# Revit family: HFS
name_source: partatom
category: Duct Accessories
revit_build: Autodesk Revit 2014 (Build: 20130308_1515(x64)
units: mm (PartAtom-declared; Revit-internal decimal feet)

## types (1)
- HFS
    A = 132 mm
    A Min = 115 mm
    Actuator Material = Aluminium
    Actuator Width = 523 mm
    Array = 5
    B = 50 mm
    B Min = 33 mm
    Blade Spacing = 146 mm  [stored 0.479003 ft]
    Blade W = 466 mm  [stored 1.52887 ft]
    Blades = 5
    C = 747 mm
    C Min = 613 mm
    Frame Allowance = 23 mm  [stored 0.0754593 ft]
    Frame Edge = 6 mm  [stored 0.019685 ft]
    Frame Material = Aluminium
    H Min = 814 mm  [stored 2.6706 ft]
    Internal Duct H = 894 mm
    Internal Duct W = 494 mm
    Manufacturer = Holyoake Industries
    Model = HFS
    Mounting Frame Material = Aluminium
    Multiple Blade = Yes
    Nominal H = 900 mm  [stored 2.95276 ft]
    Nominal W = 500 mm  [stored 1.64042 ft]
    Parametric H = 900 mm  [stored 2.95276 ft]
    Parametric W = 500 mm  [stored 1.64042 ft]
    Single Blade = No
    URL = http://www.productspec.net

note: [stored X ft] marks values corroborated as IEEE doubles in the binary element streams (Revit-internal decimal feet)

## geometry (parser evidence)
native form markers: Sweep x8
no freeform markers — native parametric forms only
